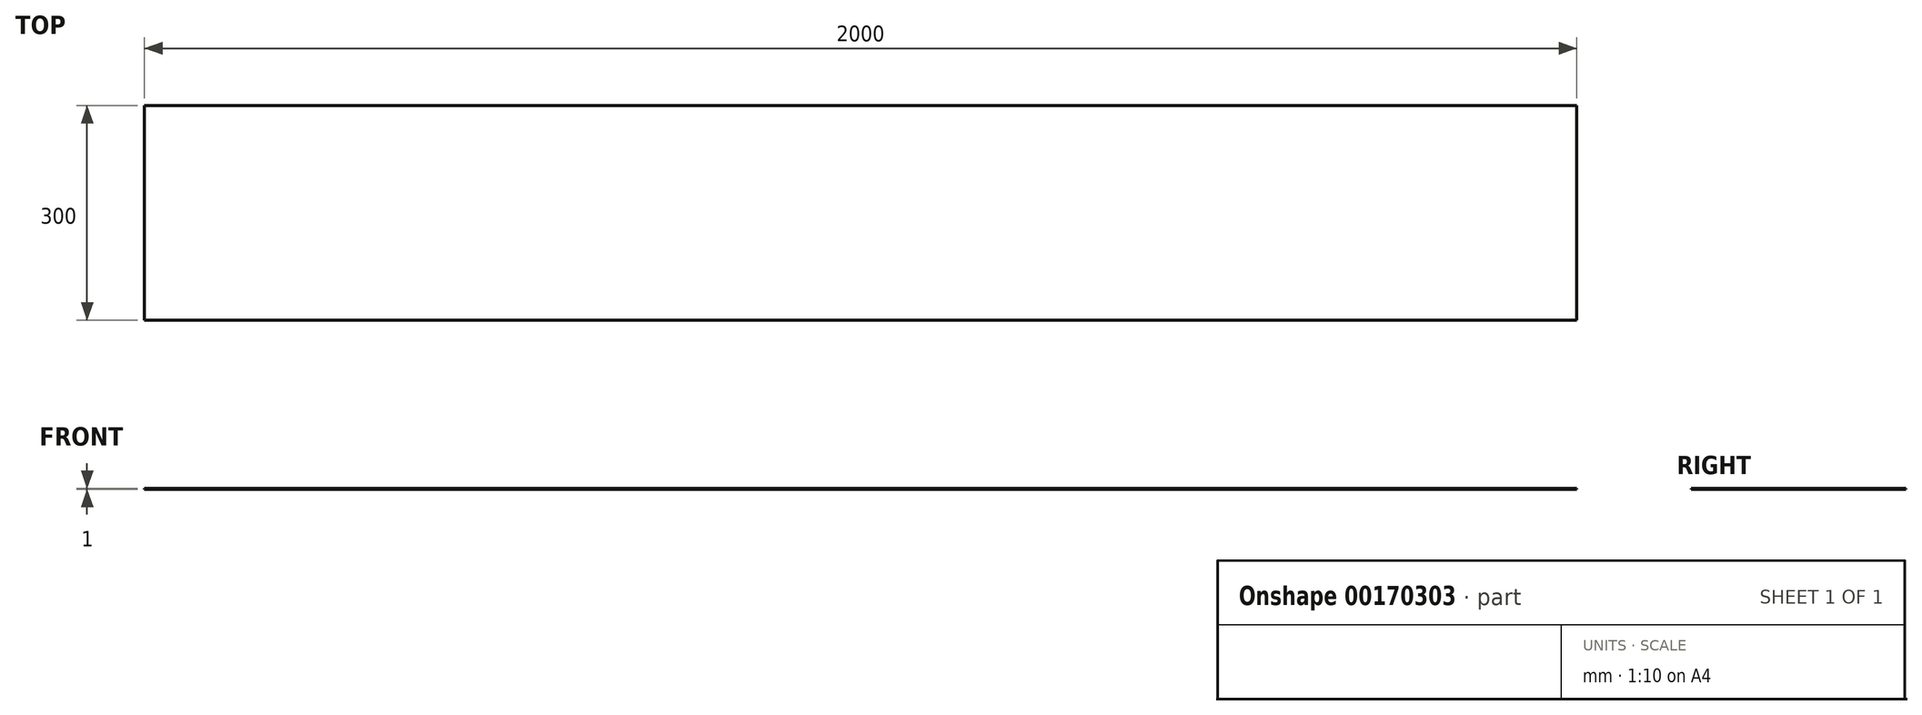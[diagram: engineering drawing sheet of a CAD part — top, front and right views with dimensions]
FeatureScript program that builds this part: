
annotation { "Feature Type Name" : "Feature", "Feature Type Description" : "" }
export const myFeature = defineFeature(function(context is Context, id is Id, definition is map)
    precondition{}
    {
        {
            var Q0;
            Q0=qCreatedBy(makeId("Top.planeOp"),FACE);
            var sketch = newSketch(context, id + "F0", { "sketchPlane" : qUnion([Q0])});
            skLineSegment(sketch, "E0.bottom", {"start": v(-338.54, 209.64) * mm, "end": v(61.46, 209.64) * mm});
            skLineSegment(sketch, "E0.top", {"start": v(-338.54, -90.36) * mm, "end": v(61.46, -90.36) * mm});
            skLineSegment(sketch, "E0.left", {"start": v(-338.54, 209.64) * mm, "end": v(-338.54, -90.36) * mm});
            skLineSegment(sketch, "E0.right", {"start": v(61.46, 209.64) * mm, "end": v(61.46, -90.36) * mm});
            skLineSegment(sketch, "E1.bottom", {"start": v(61.46, 209.64) * mm, "end": v(461.46, 209.64) * mm});
            skLineSegment(sketch, "E1.top", {"start": v(61.46, -90.36) * mm, "end": v(461.46, -90.36) * mm});
            skLineSegment(sketch, "E1.right", {"start": v(461.46, 209.64) * mm, "end": v(461.46, -90.36) * mm});
            skLineSegment(sketch, "E2.bottom", {"start": v(-338.54, 209.64) * mm, "end": v(-738.54, 209.64) * mm});
            skLineSegment(sketch, "E2.top", {"start": v(-338.54, -90.36) * mm, "end": v(-738.54, -90.36) * mm});
            skLineSegment(sketch, "E2.right", {"start": v(-738.54, 209.64) * mm, "end": v(-738.54, -90.36) * mm});
            skLineSegment(sketch, "E3.bottom", {"start": v(461.46, 209.64) * mm, "end": v(861.46, 209.64) * mm});
            skLineSegment(sketch, "E3.top", {"start": v(461.46, -90.36) * mm, "end": v(861.46, -90.36) * mm});
            skLineSegment(sketch, "E3.right", {"start": v(861.46, 209.64) * mm, "end": v(861.46, -90.36) * mm});
            skLineSegment(sketch, "E4.bottom", {"start": v(-738.54, 209.64) * mm, "end": v(-1138.54, 209.64) * mm});
            skLineSegment(sketch, "E4.top", {"start": v(-738.54, -90.36) * mm, "end": v(-1138.54, -90.36) * mm});
            skLineSegment(sketch, "E4.right", {"start": v(-1138.54, 209.64) * mm, "end": v(-1138.54, -90.36) * mm});
            skSolve(sketch);
        }
        {
            var Q0;
            Q0 = qSketchRegion(id + "F0", true);
            extrude(context, id + "F1", {"entities" : qUnion([Q0]), "depth" : 1 * mm});
        }
    });
